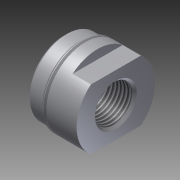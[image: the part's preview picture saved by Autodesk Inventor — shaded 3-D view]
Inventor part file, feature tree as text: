
AUTODESK INVENTOR PART (.ipt)
format: ipt  version: 2012 (Build 160160000, 160)  size: 206,848 bytes
history: native  units: in
note: dims shown in document units (in); Inventor stores cm internally (conversion verified against a paired STEP export)
features: other x112, sketch x4, revolve x3, thread x1, extrude x1
ambient origin geometry x8: Origin, YZ Plane, XZ Plane, XY Plane, X Axis, Y Axis, Z Axis, Center Point
bodies: Solid1 (feature_tree)
feature tree (121):
  revolve  "Revolution1"  Angle=360.0deg
  revolve  "Revolution2"  [1 undecoded]
  thread  "Thread1"  [1 undecoded]
  extrude  "Extrusion1"  [1 undecoded]
  revolve  "Revolution3"  [1 undecoded]
  other  "cut1_XY"
  other  "cut1_YZ"
  other  "cut1_ZX"
  other  "cut1_X"
  other  "cut1_Y"
  other  "cut1_Z"
  other  "cut1_Center"
  other  "cut2_XY"
  other  "cut2_YZ"
  other  "cut2_ZX"
  other  "cut2_X"
  other  "cut2_Y"
  other  "cut2_Z"
  other  "cut2_Center"
  other  "to_tube_XY"
  other  "to_tube_YZ"
  other  "to_tube_ZX"
  other  "to_tube_X"
  other  "to_tube_Y"
  other  "to_tube_Z"
  other  "to_tube_Center"
  other  "lovra_XY"
  other  "lovra_YZ"
  other  "lovra_ZX"
  other  "lovra_X"
  other  "lovra_Y"
  other  "lovra_Z"
  other  "lovra_Center"
  other  "to_nut_XY"
  other  "to_nut_YZ"
  other  "to_nut_ZX"
  other  "to_nut_X"
  other  "to_nut_Y"
  other  "to_nut_Z"
  other  "to_nut_Center"
  other  "lovra1_XY"
  other  "lovra1_YZ"
  other  "lovra1_ZX"
  other  "lovra1_X"
  other  "lovra1_Y"
  other  "lovra1_Z"
  other  "lovra1_Center"
  other  "lovra2_XY"
  other  "lovra2_YZ"
  other  "lovra2_ZX"
  other  "lovra2_X"
  other  "lovra2_Y"
  other  "lovra2_Z"
  other  "lovra2_Center"
  other  "lovra3_XY"
  other  "lovra3_YZ"
  other  "lovra3_ZX"
  other  "lovra3_X"
  other  "lovra3_Y"
  other  "lovra3_Z"
  other  "lovra3_Center"
  other  "to_pin_XY"
  other  "to_pin_YZ"
  other  "to_pin_ZX"
  other  "to_pin_X"
  other  "to_pin_Y"
  other  "to_pin_Z"
  other  "to_pin_Center"
  other  "olen_XY"
  other  "olen_YZ"
  other  "olen_ZX"
  other  "olen_X"
  other  "olen_Y"
  other  "olen_Z"
  other  "olen_Center"
  other  "cutf1_XY"
  other  "cutf1_YZ"
  other  "cutf1_ZX"
  other  "cutf1_X"
  other  "cutf1_Y"
  other  "cutf1_Z"
  other  "cutf1_Center"
  other  "cutf2_XY"
  other  "cutf2_YZ"
  other  "cutf2_ZX"
  other  "cutf2_X"
  other  "cutf2_Y"
  other  "cutf2_Z"
  other  "cutf2_Center"
  other  "lovra21_XY"
  other  "lovra21_YZ"
  other  "lovra21_ZX"
  other  "lovra21_X"
  other  "lovra21_Y"
  other  "lovra21_Z"
  other  "lovra21_Center"
  other  "lovra22_XY"
  other  "lovra22_YZ"
  other  "lovra22_ZX"
  other  "lovra22_X"
  other  "lovra22_Y"
  other  "lovra22_Z"
  other  "lovra22_Center"
  other  "to_screw_XY"
  other  "to_screw_YZ"
  other  "to_screw_ZX"
  other  "to_screw_X"
  other  "to_screw_Y"
  other  "to_screw_Z"
  other  "to_screw_Center"
  other  "to_mounting_bracket_XY"
  other  "to_mounting_bracket_YZ"
  other  "to_mounting_bracket_ZX"
  other  "to_mounting_bracket_X"
  other  "to_mounting_bracket_Y"
  other  "to_mounting_bracket_Z"
  other  "to_mounting_bracket_Center"
  sketch  "Sketch_1"  dims[d0=360.0deg d1=360.0deg]
  sketch  "Sketch_6"
  sketch  "Sketch_5"  dims[d2=0.302in d3=0.2285in d4=0.188in d5=0.0in d6=360.0deg]
  sketch  "Sketch_24"
note: 4 required parameter values undecoded (feature->parameter linkage not recoverable at this tier; creation-order binding heuristic only, values carry confidence <= 0.55)